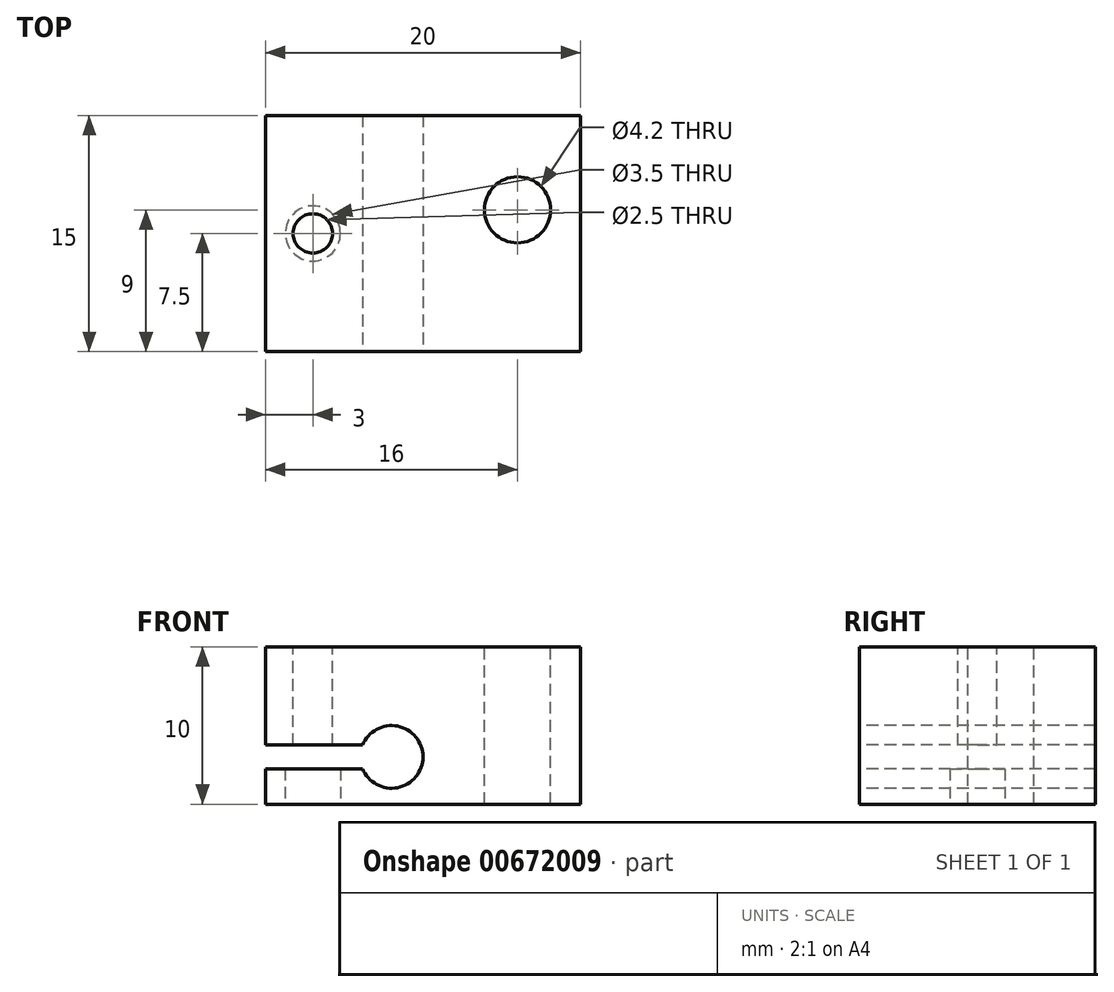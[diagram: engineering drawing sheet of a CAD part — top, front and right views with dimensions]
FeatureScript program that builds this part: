
annotation { "Feature Type Name" : "Feature", "Feature Type Description" : "" }
export const myFeature = defineFeature(function(context is Context, id is Id, definition is map)
    precondition{}
    {
        {
            var Q0;
            Q0=qCreatedBy(makeId("Top.planeOp"),FACE);
            var sketch = newSketch(context, id + "F0", { "sketchPlane" : qUnion([Q0])});
            skLineSegment(sketch, "E0.bottom", {"start": v(10, 7.5) * mm, "end": v(-10, 7.5) * mm});
            skLineSegment(sketch, "E0.top", {"start": v(10, -7.5) * mm, "end": v(-10, -7.5) * mm});
            skLineSegment(sketch, "E0.left", {"start": v(10, 7.5) * mm, "end": v(10, -7.5) * mm});
            skLineSegment(sketch, "E0.right", {"start": v(-10, 7.5) * mm, "end": v(-10, -7.5) * mm});
            skPoint(sketch, "E0.middle", {"position": v(0, 0) * mm});
            skSolve(sketch);
        }
        {
            var Q0;
            Q0=makeQuery(id+"F0.imprint","IMPRINT",FACE,{"disambiguationData":[TD([[makeQuery(id+"F0.imprint","IMPRINT",EDGE,{"derivedFrom":sQuery(id+"F0.wireOp",EDGE,"E0.bottom")}),1.0]])]});
            extrude(context, id + "F1", {"entities" : qUnion([Q0]), "depth" : 10 * mm, "offsetDistance" : 25 * mm});
        }
        {
            var Q0;
            Q0=makeQuery(id+"F1.opExtrude","CAP_FACE",FACE,{"disambiguationData":[OSD([sQuery(id+"F0.wireOp",EDGE,"E0.bottom"),sQuery(id+"F0.wireOp",EDGE,"E0.top"),sQuery(id+"F0.wireOp",EDGE,"E0.left"),sQuery(id+"F0.wireOp",EDGE,"E0.right")])],"isStart":false});
            var sketch = newSketch(context, id + "F2", { "sketchPlane" : qUnion([Q0])});
            skPoint(sketch, "E1", {"position": v(6, 1.5) * mm});
            skSolve(sketch);
        }
        {
            var Q0;
            Q0=sQuery(id+"F2.wireOp",VERTEX,"E1");
            var Q1;
            Q1=makeQuery(id+"F1.opExtrude","SWEPT_BODY",BODY,{"disambiguationData":[OSD([sQuery(id+"F0.wireOp",EDGE,"E0.bottom"),sQuery(id+"F0.wireOp",EDGE,"E0.top"),sQuery(id+"F0.wireOp",EDGE,"E0.left"),sQuery(id+"F0.wireOp",EDGE,"E0.right")])]});
            hole(context, id + "F3", {"style" : HoleStyle.SIMPLE, "endStyle" : HoleEndStyle.THROUGH, "standardTappedOrClearance" : lookupTablePath({ "standard" : "ISO", "engagement" : "75%", "pitch" : "0.8 mm", "size" : "M5", "type" : "Tapped" }), "standardBlindInLast" : lookupTablePath({ "standard" : "ISO", "engagement" : "75%", "pitch" : "0.8 mm", "size" : "M5", "type" : "Tapped" }), "holeDiameter" : 4.2 * mm, "majorDiameter" : 5 * mm, "showTappedDepth" : true, "isTappedThrough" : true, "tappedDepth" : 7.6 * mm, "tapClearance" : 3, "startFromSketch" : true, "locations" : qUnion([Q0]), "scope" : qUnion([Q1])});
        }
        {
            var Q0;
            Q0=makeQuery(id+"F1.opExtrude","SWEPT_FACE",FACE,{"disambiguationData":[OSD([sQuery(id+"F0.wireOp",EDGE,"E0.top")])]});
            var sketch = newSketch(context, id + "F4", { "sketchPlane" : qUnion([Q0])});
            skCircle(sketch, "E2", {"center": v(-2, 3) * mm, "radius": 2 * mm});
            skLineSegment(sketch, "E3", {"start": v(-10, 3.75) * mm, "end": v(-3.84, 3.75) * mm});
            skLineSegment(sketch, "E4", {"start": v(-10, 2.25) * mm, "end": v(-3.84, 2.25) * mm});
            skLineSegment(sketch, "E5", {"start": v(-2, 3) * mm, "end": v(-11.07, 3) * mm, "construction": true});
            skSolve(sketch);
        }
        {
            var Q0;
            {var subQ0=sQuery(id+"F4.wireOp",EDGE,"E2");var subQ1=makeQuery(id+"F4.imprint","INTERSECT",VERTEX,{"derivedFrom":[subQ0,sQuery(id+"F4.wireOp",EDGE,"E3")]});Q0=makeQuery(id+"F4.imprint","IMPRINT",FACE,{"disambiguationData":[TD([[makeQuery(id+"F4.imprint","IMPRINT",EDGE,{"disambiguationData":[TD([[subQ1,-1.0]])],"derivedFrom":subQ0}),1.0]])]});}
            var Q1;
            {var subQ0=sQuery(id+"F4.wireOp",EDGE,"E3");Q1=makeQuery(id+"F4.imprint","IMPRINT",FACE,{"disambiguationData":[TD([[makeQuery(id+"F4.imprint","IMPRINT",EDGE,{"derivedFrom":subQ0}),-1.0]])]});}
            extrude(context, id + "F5", {"entities" : qUnion([Q0, Q1]), "operationType" : NewBodyOperationType.REMOVE, "endBound" : BoundingType.THROUGH_ALL, "oppositeDirection" : true, "depth" : 25 * mm, "offsetDistance" : 25 * mm});
        }
        {
            var Q0;
            Q0=makeQuery(id+"F1.opExtrude","CAP_FACE",FACE,{"disambiguationData":[OSD([sQuery(id+"F0.wireOp",EDGE,"E0.bottom"),sQuery(id+"F0.wireOp",EDGE,"E0.top"),sQuery(id+"F0.wireOp",EDGE,"E0.left"),sQuery(id+"F0.wireOp",EDGE,"E0.right")])],"isStart":true});
            var sketch = newSketch(context, id + "F6", { "sketchPlane" : qUnion([Q0])});
            skPoint(sketch, "E6", {"position": v(-7, 0) * mm});
            skSolve(sketch);
        }
        {
            var Q0;
            Q0=sQuery(id+"F6.wireOp",VERTEX,"E6");
            var Q1;
            Q1=makeQuery(id+"F1.opExtrude","SWEPT_BODY",BODY,{"disambiguationData":[OSD([sQuery(id+"F0.wireOp",EDGE,"E0.bottom"),sQuery(id+"F0.wireOp",EDGE,"E0.top"),sQuery(id+"F0.wireOp",EDGE,"E0.left"),sQuery(id+"F0.wireOp",EDGE,"E0.right")])]});
            hole(context, id + "F7", {"style" : HoleStyle.SIMPLE, "endStyle" : HoleEndStyle.BLIND, "holeDiameter" : 3.5 * mm, "majorDiameter" : 5 * mm, "holeDepth" : 3 * mm, "isTappedThrough" : true, "tappedDepth" : 7.6 * mm, "tapClearance" : 3, "startFromSketch" : true, "locations" : qUnion([Q0]), "scope" : qUnion([Q1])});
        }
        {
            var Q0;
            Q0=makeQuery(id+"F1.opExtrude","CAP_FACE",FACE,{"disambiguationData":[OSD([sQuery(id+"F0.wireOp",EDGE,"E0.bottom"),sQuery(id+"F0.wireOp",EDGE,"E0.top"),sQuery(id+"F0.wireOp",EDGE,"E0.left"),sQuery(id+"F0.wireOp",EDGE,"E0.right")])],"isStart":false});
            var sketch = newSketch(context, id + "F8", { "sketchPlane" : qUnion([Q0])});
            skPoint(sketch, "E7", {"position": v(-7, 0) * mm});
            skPoint(sketch, "E7.positionSnap0", {"position": v(-10, 0) * mm});
            skSolve(sketch);
        }
        {
            var Q0;
            Q0=sQuery(id+"F8.wireOp",VERTEX,"E7");
            var Q1;
            Q1=makeQuery(id+"F1.opExtrude","SWEPT_BODY",BODY,{"disambiguationData":[OSD([sQuery(id+"F0.wireOp",EDGE,"E0.bottom"),sQuery(id+"F0.wireOp",EDGE,"E0.top"),sQuery(id+"F0.wireOp",EDGE,"E0.left"),sQuery(id+"F0.wireOp",EDGE,"E0.right")])]});
            hole(context, id + "F9", {"style" : HoleStyle.SIMPLE, "endStyle" : HoleEndStyle.THROUGH, "standardTappedOrClearance" : lookupTablePath({ "standard" : "ISO", "engagement" : "75%", "pitch" : "0.5 mm", "size" : "M3", "type" : "Tapped" }), "standardBlindInLast" : lookupTablePath({ "standard" : "ISO", "engagement" : "75%", "pitch" : "0.5 mm", "size" : "M3", "type" : "Tapped" }), "holeDiameter" : 2.5 * mm, "majorDiameter" : 3 * mm, "showTappedDepth" : true, "isTappedThrough" : true, "tappedDepth" : 7.6 * mm, "tapClearance" : 3, "startFromSketch" : true, "locations" : qUnion([Q0]), "scope" : qUnion([Q1])});
        }
    });
